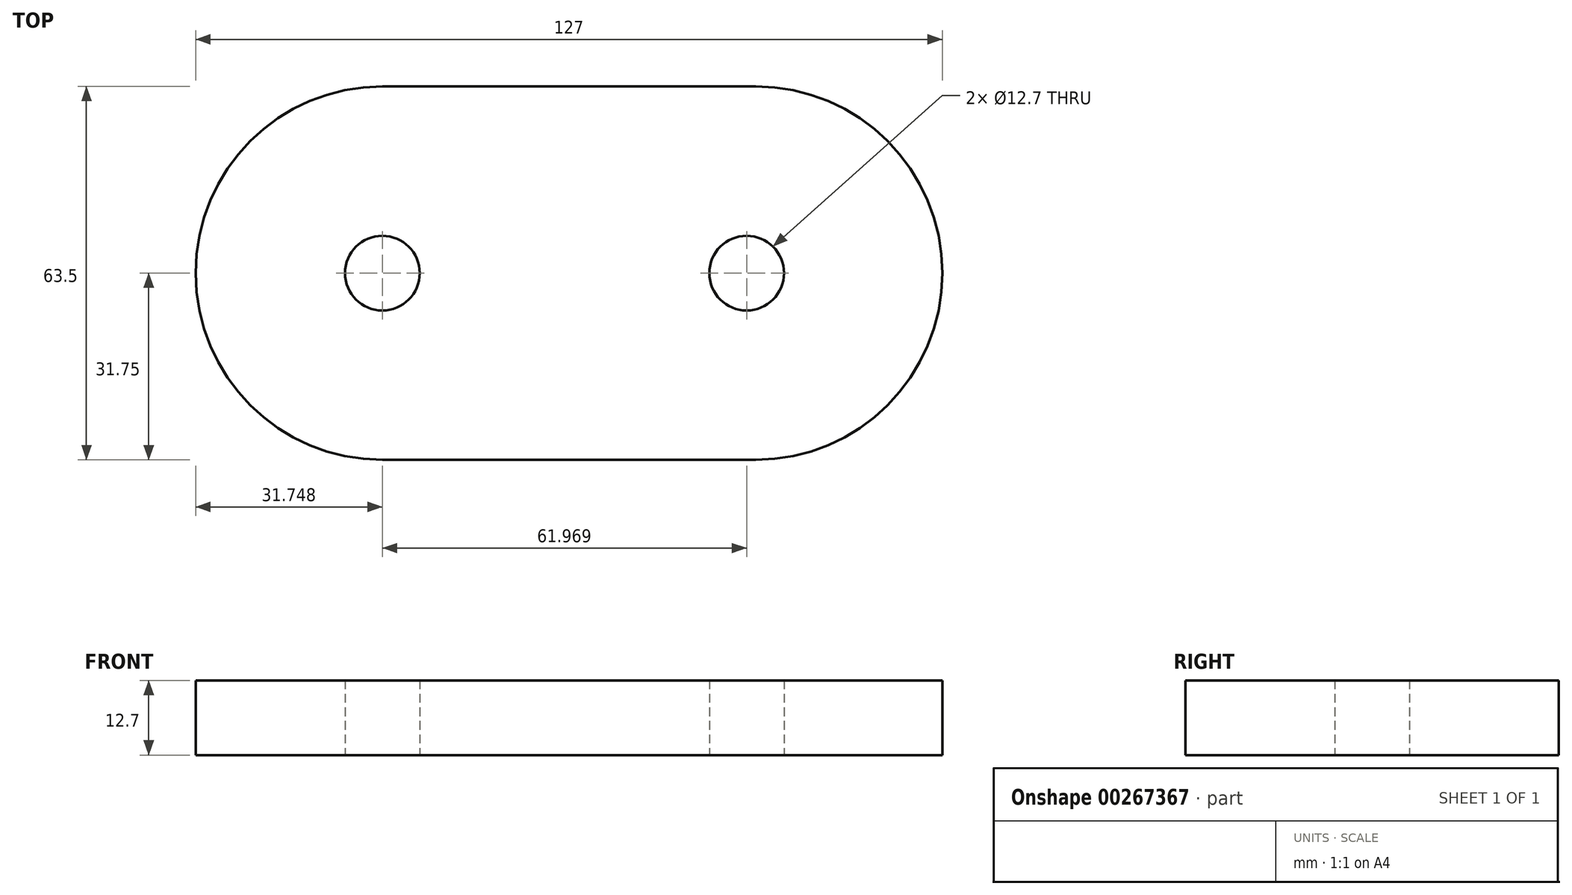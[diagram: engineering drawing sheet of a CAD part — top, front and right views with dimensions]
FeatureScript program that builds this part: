
annotation { "Feature Type Name" : "Feature", "Feature Type Description" : "" }
export const myFeature = defineFeature(function(context is Context, id is Id, definition is map)
    precondition{}
    {
        {
            var Q0;
            Q0=qCreatedBy(makeId("Top.planeOp"),FACE);
            var sketch = newSketch(context, id + "F0", { "sketchPlane" : qUnion([Q0])});
            skArc(sketch, "E0", {"start": v(-62.04, 31.75) * mm, "mid": v(-93.8, 0) * mm, "end": v(-62.04, -31.75) * mm});
            skArc(sketch, "E1", {"start": v(1.46, -31.75) * mm, "mid": v(33.2, 0) * mm, "end": v(1.46, 31.75) * mm});
            skLineSegment(sketch, "E2", {"start": v(-62.04, 31.75) * mm, "end": v(1.46, 31.75) * mm});
            skLineSegment(sketch, "E3", {"start": v(-62.04, -31.75) * mm, "end": v(1.46, -31.75) * mm});
            skPoint(sketch, "E4.end.orphan", {"position": v(-62.04, 31.75) * mm});
            skCircle(sketch, "E5", {"center": v(-62.04, 0) * mm, "radius": 6.35 * mm});
            skCircle(sketch, "E6", {"center": v(-0.07, 0) * mm, "radius": 6.35 * mm});
            skSolve(sketch);
        }
        {
            var Q0;
            Q0=makeQuery(id+"F0.imprint","IMPRINT",FACE,{"disambiguationData":[TD([[makeQuery(id+"F0.imprint","IMPRINT",EDGE,{"derivedFrom":sQuery(id+"F0.wireOp",EDGE,"E0")}),1.0]])]});
            extrude(context, id + "F1", {"entities" : qUnion([Q0]), "depth" : 12.7 * mm});
        }
    });
